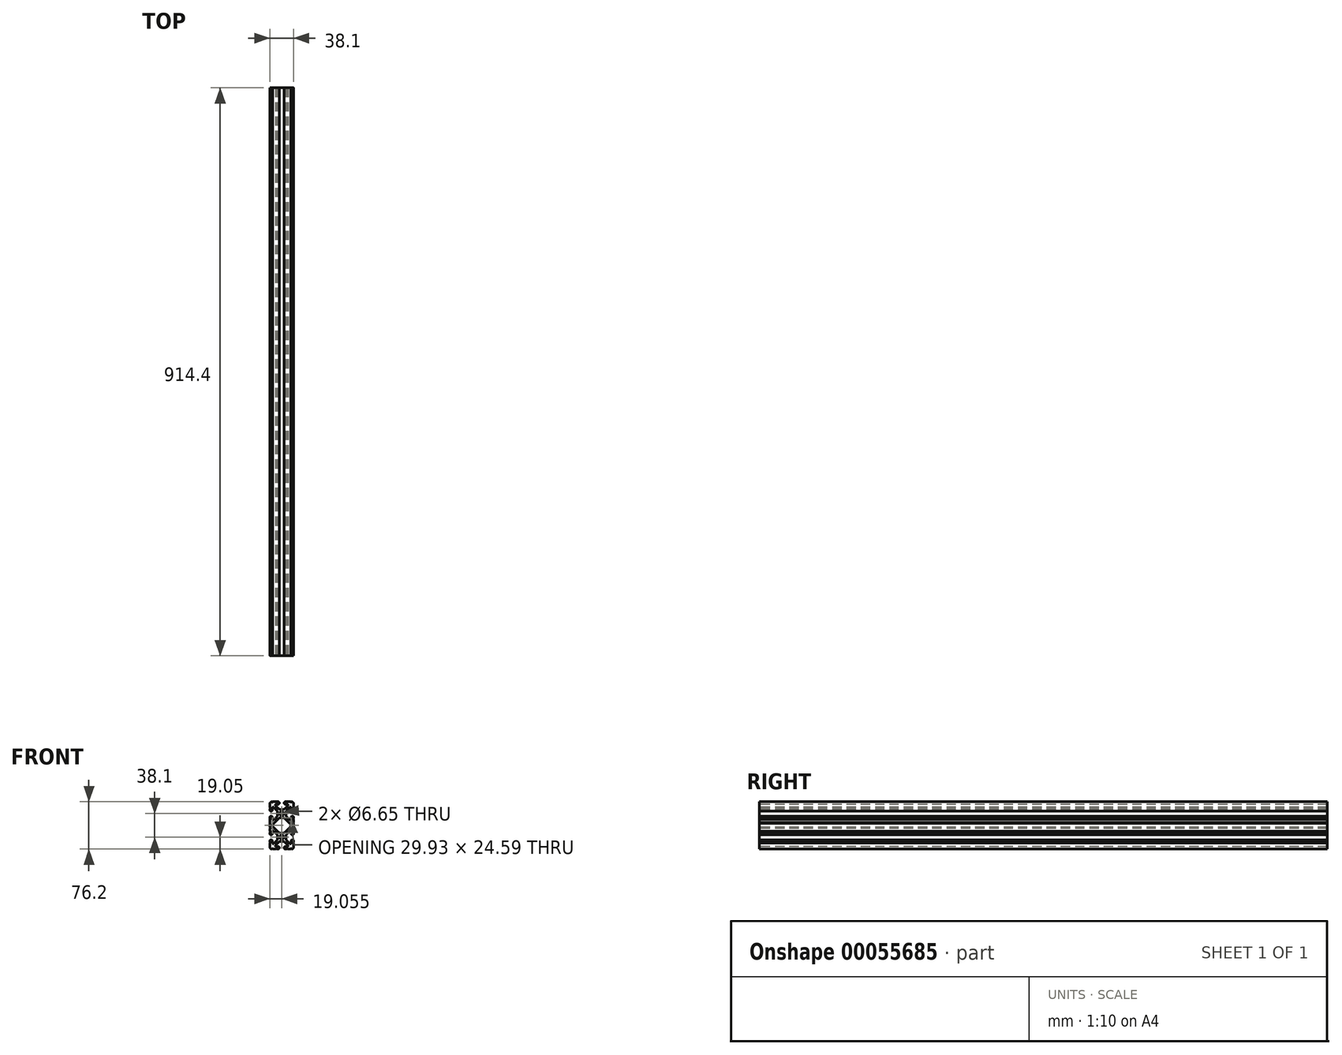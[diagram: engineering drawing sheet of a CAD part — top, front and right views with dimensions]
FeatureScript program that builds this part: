
annotation { "Feature Type Name" : "Feature", "Feature Type Description" : "" }
export const myFeature = defineFeature(function(context is Context, id is Id, definition is map)
    precondition{}
    {
        {
            var Q0;
            Q0=qCreatedBy(makeId("Front.planeOp"),FACE);
            var sketch = newSketch(context, id + "F0", { "sketchPlane" : qUnion([Q0])});
            skLineSegment(sketch, "E0", {"start": v(-110.84, 69.05) * mm, "end": v(-103.85, 69.05) * mm});
            skLineSegment(sketch, "E1", {"start": v(-107.35, 65.56) * mm, "end": v(-107.35, 72.54) * mm});
            skLineSegment(sketch, "E2", {"start": v(-110.84, 30.95) * mm, "end": v(-103.85, 30.95) * mm});
            skLineSegment(sketch, "E3", {"start": v(-107.35, 27.46) * mm, "end": v(-107.35, 34.44) * mm});
            skLineSegment(sketch, "E4", {"start": v(-89.1, 46.04) * mm, "end": v(-87.5, 46.04) * mm});
            skLineSegment(sketch, "E5", {"start": v(-88.3, 45.24) * mm, "end": v(-88.3, 46.84) * mm});
            skLineSegment(sketch, "E6", {"start": v(-99.4, 88.1) * mm, "end": v(-97.8, 88.1) * mm});
            skLineSegment(sketch, "E7", {"start": v(-98.6, 87.3) * mm, "end": v(-98.6, 88.9) * mm});
            skLineSegment(sketch, "E8", {"start": v(-127.2, 15.86) * mm, "end": v(-125.6, 15.86) * mm});
            skLineSegment(sketch, "E9", {"start": v(-126.4, 15.06) * mm, "end": v(-126.4, 16.66) * mm});
            skLineSegment(sketch, "E10", {"start": v(-89.1, 77.79) * mm, "end": v(-87.5, 77.79) * mm});
            skLineSegment(sketch, "E11", {"start": v(-88.3, 76.99) * mm, "end": v(-88.3, 78.59) * mm});
            skLineSegment(sketch, "E12", {"start": v(-127.2, 60.31) * mm, "end": v(-125.6, 60.31) * mm});
            skLineSegment(sketch, "E13", {"start": v(-126.4, 59.51) * mm, "end": v(-126.4, 61.11) * mm});
            skLineSegment(sketch, "E14", {"start": v(-89.1, 84.14) * mm, "end": v(-87.5, 84.14) * mm});
            skLineSegment(sketch, "E15", {"start": v(-88.3, 83.34) * mm, "end": v(-88.3, 84.94) * mm});
            skLineSegment(sketch, "E16", {"start": v(-127.2, 84.14) * mm, "end": v(-125.6, 84.14) * mm});
            skLineSegment(sketch, "E17", {"start": v(-126.4, 83.34) * mm, "end": v(-126.4, 84.94) * mm});
            skLineSegment(sketch, "E18", {"start": v(-127.2, 53.96) * mm, "end": v(-125.6, 53.96) * mm});
            skLineSegment(sketch, "E19", {"start": v(-126.4, 53.16) * mm, "end": v(-126.4, 54.76) * mm});
            skLineSegment(sketch, "E20", {"start": v(-116.88, 88.1) * mm, "end": v(-115.28, 88.1) * mm});
            skLineSegment(sketch, "E21", {"start": v(-116.08, 87.3) * mm, "end": v(-116.08, 88.9) * mm});
            skLineSegment(sketch, "E22", {"start": v(-89.1, 15.86) * mm, "end": v(-87.5, 15.86) * mm});
            skLineSegment(sketch, "E23", {"start": v(-88.3, 15.06) * mm, "end": v(-88.3, 16.66) * mm});
            skArc(sketch, "E24", {"start": v(-109.26, 62.3) * mm, "mid": v(-111.08, 61.93) * mm, "end": v(-112.62, 60.9) * mm});
            skLineSegment(sketch, "E25", {"start": v(-112.62, 60.9) * mm, "end": v(-121.46, 52.07) * mm});
            skArc(sketch, "E26", {"start": v(-121.46, 52.07) * mm, "mid": v(-122.31, 50) * mm, "end": v(-121.46, 47.93) * mm});
            skLineSegment(sketch, "E27", {"start": v(-121.46, 47.93) * mm, "end": v(-112.62, 39.1) * mm});
            skArc(sketch, "E28", {"start": v(-112.62, 39.1) * mm, "mid": v(-111.08, 38.07) * mm, "end": v(-109.26, 37.7) * mm});
            skLineSegment(sketch, "E29", {"start": v(-109.26, 37.7) * mm, "end": v(-105.43, 37.7) * mm});
            skArc(sketch, "E30", {"start": v(-105.43, 37.7) * mm, "mid": v(-103.61, 38.07) * mm, "end": v(-102.07, 39.1) * mm});
            skLineSegment(sketch, "E31", {"start": v(-102.07, 39.1) * mm, "end": v(-93.23, 47.93) * mm});
            skArc(sketch, "E32", {"start": v(-93.23, 47.93) * mm, "mid": v(-92.38, 50) * mm, "end": v(-93.23, 52.07) * mm});
            skLineSegment(sketch, "E33", {"start": v(-93.23, 52.07) * mm, "end": v(-102.07, 60.9) * mm});
            skArc(sketch, "E34", {"start": v(-102.07, 60.9) * mm, "mid": v(-103.61, 61.93) * mm, "end": v(-105.43, 62.3) * mm});
            skArc(sketch, "E35", {"start": v(-123.2, 88.1) * mm, "mid": v(-122.43, 87.34) * mm, "end": v(-121.67, 88.1) * mm});
            skLineSegment(sketch, "E36", {"start": v(-116.84, 88.1) * mm, "end": v(-121.67, 88.1) * mm});
            skArc(sketch, "E37", {"start": v(-116.84, 88.1) * mm, "mid": v(-116.08, 87.34) * mm, "end": v(-115.32, 88.1) * mm});
            skLineSegment(sketch, "E38", {"start": v(-112.98, 88.1) * mm, "end": v(-115.32, 88.1) * mm});
            skArc(sketch, "E39", {"start": v(-111.4, 86.53) * mm, "mid": v(-111.87, 87.64) * mm, "end": v(-112.98, 88.1) * mm});
            skLineSegment(sketch, "E40", {"start": v(-111.4, 85.61) * mm, "end": v(-111.4, 86.53) * mm});
            skArc(sketch, "E41", {"start": v(-112.98, 84.04) * mm, "mid": v(-111.87, 84.5) * mm, "end": v(-111.4, 85.61) * mm});
            skLineSegment(sketch, "E42", {"start": v(-116.74, 84.04) * mm, "end": v(-112.98, 84.04) * mm});
            skArc(sketch, "E43", {"start": v(-116.74, 84.04) * mm, "mid": v(-117.37, 83.78) * mm, "end": v(-117.63, 83.15) * mm});
            skLineSegment(sketch, "E44", {"start": v(-117.63, 82.58) * mm, "end": v(-117.63, 83.15) * mm});
            skArc(sketch, "E45", {"start": v(-117.63, 82.58) * mm, "mid": v(-117.56, 82.24) * mm, "end": v(-117.37, 81.95) * mm});
            skLineSegment(sketch, "E46", {"start": v(-112.62, 77.2) * mm, "end": v(-117.37, 81.95) * mm});
            skArc(sketch, "E47", {"start": v(-112.62, 77.2) * mm, "mid": v(-111.08, 76.17) * mm, "end": v(-109.26, 75.8) * mm});
            skLineSegment(sketch, "E48", {"start": v(-105.43, 75.8) * mm, "end": v(-109.26, 75.8) * mm});
            skArc(sketch, "E49", {"start": v(-105.43, 75.8) * mm, "mid": v(-103.61, 76.17) * mm, "end": v(-102.07, 77.2) * mm});
            skLineSegment(sketch, "E50", {"start": v(-97.32, 81.95) * mm, "end": v(-102.07, 77.2) * mm});
            skArc(sketch, "E51", {"start": v(-97.32, 81.95) * mm, "mid": v(-97.13, 82.24) * mm, "end": v(-97.06, 82.58) * mm});
            skLineSegment(sketch, "E52", {"start": v(-97.06, 83.15) * mm, "end": v(-97.06, 82.58) * mm});
            skArc(sketch, "E53", {"start": v(-97.06, 83.15) * mm, "mid": v(-97.32, 83.78) * mm, "end": v(-97.95, 84.04) * mm});
            skLineSegment(sketch, "E54", {"start": v(-101.7, 84.04) * mm, "end": v(-97.95, 84.04) * mm});
            skArc(sketch, "E55", {"start": v(-103.28, 85.61) * mm, "mid": v(-102.82, 84.5) * mm, "end": v(-101.7, 84.04) * mm});
            skLineSegment(sketch, "E56", {"start": v(-103.28, 86.53) * mm, "end": v(-103.28, 85.61) * mm});
            skArc(sketch, "E57", {"start": v(-101.7, 88.1) * mm, "mid": v(-102.82, 87.64) * mm, "end": v(-103.28, 86.53) * mm});
            skLineSegment(sketch, "E58", {"start": v(-99.37, 88.1) * mm, "end": v(-101.7, 88.1) * mm});
            skArc(sketch, "E59", {"start": v(-99.37, 88.1) * mm, "mid": v(-98.6, 87.34) * mm, "end": v(-97.85, 88.1) * mm});
            skLineSegment(sketch, "E60", {"start": v(-93.02, 88.1) * mm, "end": v(-97.85, 88.1) * mm});
            skArc(sketch, "E61", {"start": v(-93.02, 88.1) * mm, "mid": v(-92.26, 87.34) * mm, "end": v(-91.5, 88.1) * mm});
            skArc(sketch, "E62", {"start": v(-88.3, 84.9) * mm, "mid": v(-89.23, 87.17) * mm, "end": v(-91.5, 88.1) * mm});
            skArc(sketch, "E63", {"start": v(-88.3, 84.9) * mm, "mid": v(-89.06, 84.14) * mm, "end": v(-88.3, 83.38) * mm});
            skLineSegment(sketch, "E64", {"start": v(-88.3, 78.55) * mm, "end": v(-88.3, 83.38) * mm});
            skArc(sketch, "E65", {"start": v(-88.3, 78.55) * mm, "mid": v(-89.06, 77.79) * mm, "end": v(-88.3, 77.03) * mm});
            skLineSegment(sketch, "E66", {"start": v(-88.3, 74.69) * mm, "end": v(-88.3, 77.03) * mm});
            skArc(sketch, "E67", {"start": v(-89.87, 73.11) * mm, "mid": v(-88.76, 73.58) * mm, "end": v(-88.3, 74.69) * mm});
            skLineSegment(sketch, "E68", {"start": v(-90.78, 73.11) * mm, "end": v(-89.87, 73.11) * mm});
            skArc(sketch, "E69", {"start": v(-92.36, 74.69) * mm, "mid": v(-91.9, 73.58) * mm, "end": v(-90.78, 73.11) * mm});
            skLineSegment(sketch, "E70", {"start": v(-92.36, 78.45) * mm, "end": v(-92.36, 74.69) * mm});
            skArc(sketch, "E71", {"start": v(-92.36, 78.45) * mm, "mid": v(-92.62, 79.08) * mm, "end": v(-93.25, 79.34) * mm});
            skLineSegment(sketch, "E72", {"start": v(-93.82, 79.34) * mm, "end": v(-93.25, 79.34) * mm});
            skArc(sketch, "E73", {"start": v(-93.82, 79.34) * mm, "mid": v(-94.16, 79.27) * mm, "end": v(-94.44, 79.08) * mm});
            skLineSegment(sketch, "E74", {"start": v(-99.2, 74.32) * mm, "end": v(-94.44, 79.08) * mm});
            skArc(sketch, "E75", {"start": v(-99.2, 74.32) * mm, "mid": v(-100.23, 72.78) * mm, "end": v(-100.59, 70.97) * mm});
            skLineSegment(sketch, "E76", {"start": v(-100.59, 67.13) * mm, "end": v(-100.59, 70.97) * mm});
            skArc(sketch, "E77", {"start": v(-100.59, 67.13) * mm, "mid": v(-100.23, 65.32) * mm, "end": v(-99.2, 63.78) * mm});
            skLineSegment(sketch, "E78", {"start": v(-94.44, 59.02) * mm, "end": v(-99.2, 63.78) * mm});
            skArc(sketch, "E79", {"start": v(-94.44, 59.02) * mm, "mid": v(-94.16, 58.83) * mm, "end": v(-93.82, 58.76) * mm});
            skLineSegment(sketch, "E80", {"start": v(-93.25, 58.76) * mm, "end": v(-93.82, 58.76) * mm});
            skArc(sketch, "E81", {"start": v(-93.25, 58.76) * mm, "mid": v(-92.62, 59.02) * mm, "end": v(-92.36, 59.65) * mm});
            skLineSegment(sketch, "E82", {"start": v(-92.36, 63.41) * mm, "end": v(-92.36, 59.65) * mm});
            skArc(sketch, "E83", {"start": v(-90.78, 64.99) * mm, "mid": v(-91.9, 64.52) * mm, "end": v(-92.36, 63.41) * mm});
            skLineSegment(sketch, "E84", {"start": v(-89.87, 64.99) * mm, "end": v(-90.78, 64.99) * mm});
            skArc(sketch, "E85", {"start": v(-88.3, 63.41) * mm, "mid": v(-88.76, 64.52) * mm, "end": v(-89.87, 64.99) * mm});
            skLineSegment(sketch, "E86", {"start": v(-88.3, 61.07) * mm, "end": v(-88.3, 63.41) * mm});
            skArc(sketch, "E87", {"start": v(-88.3, 61.07) * mm, "mid": v(-89.06, 60.31) * mm, "end": v(-88.3, 59.55) * mm});
            skLineSegment(sketch, "E88", {"start": v(-88.3, 54.72) * mm, "end": v(-88.3, 59.55) * mm});
            skArc(sketch, "E89", {"start": v(-88.3, 54.72) * mm, "mid": v(-89.06, 53.96) * mm, "end": v(-88.3, 53.2) * mm});
            skLineSegment(sketch, "E90", {"start": v(-88.3, 46.8) * mm, "end": v(-88.3, 53.2) * mm});
            skArc(sketch, "E91", {"start": v(-88.3, 46.8) * mm, "mid": v(-89.06, 46.04) * mm, "end": v(-88.3, 45.28) * mm});
            skLineSegment(sketch, "E92", {"start": v(-88.3, 40.45) * mm, "end": v(-88.3, 45.28) * mm});
            skArc(sketch, "E93", {"start": v(-88.3, 40.45) * mm, "mid": v(-89.06, 39.69) * mm, "end": v(-88.3, 38.93) * mm});
            skLineSegment(sketch, "E94", {"start": v(-88.3, 36.59) * mm, "end": v(-88.3, 38.93) * mm});
            skArc(sketch, "E95", {"start": v(-89.87, 35.01) * mm, "mid": v(-88.76, 35.48) * mm, "end": v(-88.3, 36.59) * mm});
            skLineSegment(sketch, "E96", {"start": v(-90.78, 35.01) * mm, "end": v(-89.87, 35.01) * mm});
            skArc(sketch, "E97", {"start": v(-92.36, 36.59) * mm, "mid": v(-91.9, 35.48) * mm, "end": v(-90.78, 35.01) * mm});
            skLineSegment(sketch, "E98", {"start": v(-92.36, 40.35) * mm, "end": v(-92.36, 36.59) * mm});
            skArc(sketch, "E99", {"start": v(-92.36, 40.35) * mm, "mid": v(-92.62, 40.98) * mm, "end": v(-93.25, 41.24) * mm});
            skLineSegment(sketch, "E100", {"start": v(-93.82, 41.24) * mm, "end": v(-93.25, 41.24) * mm});
            skArc(sketch, "E101", {"start": v(-93.82, 41.24) * mm, "mid": v(-94.16, 41.17) * mm, "end": v(-94.44, 40.98) * mm});
            skLineSegment(sketch, "E102", {"start": v(-99.2, 36.22) * mm, "end": v(-94.44, 40.98) * mm});
            skArc(sketch, "E103", {"start": v(-99.2, 36.22) * mm, "mid": v(-100.23, 34.68) * mm, "end": v(-100.59, 32.87) * mm});
            skLineSegment(sketch, "E104", {"start": v(-100.59, 29.03) * mm, "end": v(-100.59, 32.87) * mm});
            skArc(sketch, "E105", {"start": v(-100.59, 29.03) * mm, "mid": v(-100.23, 27.22) * mm, "end": v(-99.2, 25.68) * mm});
            skLineSegment(sketch, "E106", {"start": v(-94.44, 20.92) * mm, "end": v(-99.2, 25.68) * mm});
            skArc(sketch, "E107", {"start": v(-94.44, 20.92) * mm, "mid": v(-94.16, 20.73) * mm, "end": v(-93.82, 20.66) * mm});
            skLineSegment(sketch, "E108", {"start": v(-93.25, 20.66) * mm, "end": v(-93.82, 20.66) * mm});
            skArc(sketch, "E109", {"start": v(-93.25, 20.66) * mm, "mid": v(-92.62, 20.92) * mm, "end": v(-92.36, 21.55) * mm});
            skLineSegment(sketch, "E110", {"start": v(-92.36, 25.31) * mm, "end": v(-92.36, 21.55) * mm});
            skArc(sketch, "E111", {"start": v(-90.78, 26.89) * mm, "mid": v(-91.9, 26.42) * mm, "end": v(-92.36, 25.31) * mm});
            skLineSegment(sketch, "E112", {"start": v(-89.87, 26.89) * mm, "end": v(-90.78, 26.89) * mm});
            skArc(sketch, "E113", {"start": v(-88.3, 25.31) * mm, "mid": v(-88.76, 26.42) * mm, "end": v(-89.87, 26.89) * mm});
            skLineSegment(sketch, "E114", {"start": v(-88.3, 22.97) * mm, "end": v(-88.3, 25.31) * mm});
            skArc(sketch, "E115", {"start": v(-88.3, 22.97) * mm, "mid": v(-89.06, 22.21) * mm, "end": v(-88.3, 21.45) * mm});
            skLineSegment(sketch, "E116", {"start": v(-88.3, 16.62) * mm, "end": v(-88.3, 21.45) * mm});
            skArc(sketch, "E117", {"start": v(-88.3, 16.62) * mm, "mid": v(-89.06, 15.86) * mm, "end": v(-88.3, 15.1) * mm});
            skArc(sketch, "E118", {"start": v(-91.5, 11.9) * mm, "mid": v(-89.23, 12.83) * mm, "end": v(-88.3, 15.1) * mm});
            skArc(sketch, "E119", {"start": v(-91.5, 11.9) * mm, "mid": v(-92.26, 12.66) * mm, "end": v(-93.02, 11.9) * mm});
            skLineSegment(sketch, "E120", {"start": v(-97.85, 11.9) * mm, "end": v(-93.02, 11.9) * mm});
            skArc(sketch, "E121", {"start": v(-97.85, 11.9) * mm, "mid": v(-98.6, 12.66) * mm, "end": v(-99.37, 11.9) * mm});
            skLineSegment(sketch, "E122", {"start": v(-101.7, 11.9) * mm, "end": v(-99.37, 11.9) * mm});
            skArc(sketch, "E123", {"start": v(-103.28, 13.47) * mm, "mid": v(-102.82, 12.36) * mm, "end": v(-101.7, 11.9) * mm});
            skLineSegment(sketch, "E124", {"start": v(-103.28, 14.39) * mm, "end": v(-103.28, 13.47) * mm});
            skArc(sketch, "E125", {"start": v(-101.7, 15.96) * mm, "mid": v(-102.82, 15.5) * mm, "end": v(-103.28, 14.39) * mm});
            skLineSegment(sketch, "E126", {"start": v(-97.95, 15.96) * mm, "end": v(-101.7, 15.96) * mm});
            skArc(sketch, "E127", {"start": v(-97.95, 15.96) * mm, "mid": v(-97.32, 16.22) * mm, "end": v(-97.06, 16.85) * mm});
            skLineSegment(sketch, "E128", {"start": v(-97.06, 17.42) * mm, "end": v(-97.06, 16.85) * mm});
            skArc(sketch, "E129", {"start": v(-97.06, 17.42) * mm, "mid": v(-97.13, 17.76) * mm, "end": v(-97.32, 18.05) * mm});
            skLineSegment(sketch, "E130", {"start": v(-102.07, 22.8) * mm, "end": v(-97.32, 18.05) * mm});
            skArc(sketch, "E131", {"start": v(-102.07, 22.8) * mm, "mid": v(-103.61, 23.83) * mm, "end": v(-105.43, 24.2) * mm});
            skLineSegment(sketch, "E132", {"start": v(-109.26, 24.2) * mm, "end": v(-105.43, 24.2) * mm});
            skArc(sketch, "E133", {"start": v(-109.26, 24.2) * mm, "mid": v(-111.08, 23.83) * mm, "end": v(-112.62, 22.8) * mm});
            skLineSegment(sketch, "E134", {"start": v(-117.37, 18.05) * mm, "end": v(-112.62, 22.8) * mm});
            skArc(sketch, "E135", {"start": v(-117.37, 18.05) * mm, "mid": v(-117.56, 17.76) * mm, "end": v(-117.63, 17.42) * mm});
            skLineSegment(sketch, "E136", {"start": v(-117.63, 16.85) * mm, "end": v(-117.63, 17.42) * mm});
            skArc(sketch, "E137", {"start": v(-117.63, 16.85) * mm, "mid": v(-117.37, 16.22) * mm, "end": v(-116.74, 15.96) * mm});
            skLineSegment(sketch, "E138", {"start": v(-112.98, 15.96) * mm, "end": v(-116.74, 15.96) * mm});
            skArc(sketch, "E139", {"start": v(-111.4, 14.39) * mm, "mid": v(-111.87, 15.5) * mm, "end": v(-112.98, 15.96) * mm});
            skLineSegment(sketch, "E140", {"start": v(-111.4, 13.47) * mm, "end": v(-111.4, 14.39) * mm});
            skArc(sketch, "E141", {"start": v(-112.98, 11.9) * mm, "mid": v(-111.87, 12.36) * mm, "end": v(-111.4, 13.47) * mm});
            skLineSegment(sketch, "E142", {"start": v(-115.32, 11.9) * mm, "end": v(-112.98, 11.9) * mm});
            skArc(sketch, "E143", {"start": v(-115.32, 11.9) * mm, "mid": v(-116.08, 12.66) * mm, "end": v(-116.84, 11.9) * mm});
            skLineSegment(sketch, "E144", {"start": v(-121.67, 11.9) * mm, "end": v(-116.84, 11.9) * mm});
            skArc(sketch, "E145", {"start": v(-121.67, 11.9) * mm, "mid": v(-122.43, 12.66) * mm, "end": v(-123.2, 11.9) * mm});
            skArc(sketch, "E146", {"start": v(-126.4, 15.1) * mm, "mid": v(-125.47, 12.83) * mm, "end": v(-123.2, 11.9) * mm});
            skArc(sketch, "E147", {"start": v(-126.4, 15.1) * mm, "mid": v(-125.63, 15.86) * mm, "end": v(-126.4, 16.62) * mm});
            skLineSegment(sketch, "E148", {"start": v(-126.4, 21.45) * mm, "end": v(-126.4, 16.62) * mm});
            skArc(sketch, "E149", {"start": v(-126.4, 21.45) * mm, "mid": v(-125.63, 22.21) * mm, "end": v(-126.4, 22.97) * mm});
            skLineSegment(sketch, "E150", {"start": v(-126.4, 25.31) * mm, "end": v(-126.4, 22.97) * mm});
            skArc(sketch, "E151", {"start": v(-124.82, 26.89) * mm, "mid": v(-125.93, 26.42) * mm, "end": v(-126.4, 25.31) * mm});
            skLineSegment(sketch, "E152", {"start": v(-123.9, 26.89) * mm, "end": v(-124.82, 26.89) * mm});
            skArc(sketch, "E153", {"start": v(-122.33, 25.31) * mm, "mid": v(-122.8, 26.42) * mm, "end": v(-123.9, 26.89) * mm});
            skLineSegment(sketch, "E154", {"start": v(-122.33, 21.55) * mm, "end": v(-122.33, 25.31) * mm});
            skArc(sketch, "E155", {"start": v(-122.33, 21.55) * mm, "mid": v(-122.07, 20.92) * mm, "end": v(-121.44, 20.66) * mm});
            skLineSegment(sketch, "E156", {"start": v(-120.87, 20.66) * mm, "end": v(-121.44, 20.66) * mm});
            skArc(sketch, "E157", {"start": v(-120.87, 20.66) * mm, "mid": v(-120.53, 20.73) * mm, "end": v(-120.25, 20.92) * mm});
            skLineSegment(sketch, "E158", {"start": v(-115.5, 25.68) * mm, "end": v(-120.25, 20.92) * mm});
            skArc(sketch, "E159", {"start": v(-115.5, 25.68) * mm, "mid": v(-114.46, 27.22) * mm, "end": v(-114.1, 29.03) * mm});
            skLineSegment(sketch, "E160", {"start": v(-114.1, 32.87) * mm, "end": v(-114.1, 29.03) * mm});
            skArc(sketch, "E161", {"start": v(-114.1, 32.87) * mm, "mid": v(-114.46, 34.68) * mm, "end": v(-115.5, 36.22) * mm});
            skLineSegment(sketch, "E162", {"start": v(-120.25, 40.98) * mm, "end": v(-115.5, 36.22) * mm});
            skArc(sketch, "E163", {"start": v(-120.25, 40.98) * mm, "mid": v(-120.53, 41.17) * mm, "end": v(-120.87, 41.24) * mm});
            skLineSegment(sketch, "E164", {"start": v(-121.44, 41.24) * mm, "end": v(-120.87, 41.24) * mm});
            skArc(sketch, "E165", {"start": v(-121.44, 41.24) * mm, "mid": v(-122.07, 40.98) * mm, "end": v(-122.33, 40.35) * mm});
            skLineSegment(sketch, "E166", {"start": v(-122.33, 36.59) * mm, "end": v(-122.33, 40.35) * mm});
            skArc(sketch, "E167", {"start": v(-123.9, 35.01) * mm, "mid": v(-122.8, 35.48) * mm, "end": v(-122.33, 36.59) * mm});
            skLineSegment(sketch, "E168", {"start": v(-124.82, 35.01) * mm, "end": v(-123.9, 35.01) * mm});
            skArc(sketch, "E169", {"start": v(-126.4, 36.59) * mm, "mid": v(-125.93, 35.48) * mm, "end": v(-124.82, 35.01) * mm});
            skLineSegment(sketch, "E170", {"start": v(-126.4, 38.93) * mm, "end": v(-126.4, 36.59) * mm});
            skArc(sketch, "E171", {"start": v(-126.4, 38.93) * mm, "mid": v(-125.63, 39.69) * mm, "end": v(-126.4, 40.45) * mm});
            skLineSegment(sketch, "E172", {"start": v(-126.4, 45.28) * mm, "end": v(-126.4, 40.45) * mm});
            skArc(sketch, "E173", {"start": v(-126.4, 45.28) * mm, "mid": v(-125.63, 46.04) * mm, "end": v(-126.4, 46.8) * mm});
            skLineSegment(sketch, "E174", {"start": v(-126.4, 53.2) * mm, "end": v(-126.4, 46.8) * mm});
            skArc(sketch, "E175", {"start": v(-126.4, 53.2) * mm, "mid": v(-125.63, 53.96) * mm, "end": v(-126.4, 54.72) * mm});
            skLineSegment(sketch, "E176", {"start": v(-126.4, 59.55) * mm, "end": v(-126.4, 54.72) * mm});
            skArc(sketch, "E177", {"start": v(-126.4, 59.55) * mm, "mid": v(-125.63, 60.31) * mm, "end": v(-126.4, 61.07) * mm});
            skLineSegment(sketch, "E178", {"start": v(-126.4, 63.41) * mm, "end": v(-126.4, 61.07) * mm});
            skArc(sketch, "E179", {"start": v(-124.82, 64.99) * mm, "mid": v(-125.93, 64.52) * mm, "end": v(-126.4, 63.41) * mm});
            skLineSegment(sketch, "E180", {"start": v(-123.9, 64.99) * mm, "end": v(-124.82, 64.99) * mm});
            skArc(sketch, "E181", {"start": v(-122.33, 63.41) * mm, "mid": v(-122.8, 64.52) * mm, "end": v(-123.9, 64.99) * mm});
            skLineSegment(sketch, "E182", {"start": v(-122.33, 59.65) * mm, "end": v(-122.33, 63.41) * mm});
            skArc(sketch, "E183", {"start": v(-122.33, 59.65) * mm, "mid": v(-122.07, 59.02) * mm, "end": v(-121.44, 58.76) * mm});
            skLineSegment(sketch, "E184", {"start": v(-120.87, 58.76) * mm, "end": v(-121.44, 58.76) * mm});
            skArc(sketch, "E185", {"start": v(-120.87, 58.76) * mm, "mid": v(-120.53, 58.83) * mm, "end": v(-120.25, 59.02) * mm});
            skLineSegment(sketch, "E186", {"start": v(-115.5, 63.78) * mm, "end": v(-120.25, 59.02) * mm});
            skArc(sketch, "E187", {"start": v(-115.5, 63.78) * mm, "mid": v(-114.46, 65.32) * mm, "end": v(-114.1, 67.13) * mm});
            skLineSegment(sketch, "E188", {"start": v(-114.1, 70.97) * mm, "end": v(-114.1, 67.13) * mm});
            skArc(sketch, "E189", {"start": v(-114.1, 70.97) * mm, "mid": v(-114.46, 72.78) * mm, "end": v(-115.5, 74.32) * mm});
            skLineSegment(sketch, "E190", {"start": v(-120.25, 79.08) * mm, "end": v(-115.5, 74.32) * mm});
            skArc(sketch, "E191", {"start": v(-120.25, 79.08) * mm, "mid": v(-120.53, 79.27) * mm, "end": v(-120.87, 79.34) * mm});
            skLineSegment(sketch, "E192", {"start": v(-121.44, 79.34) * mm, "end": v(-120.87, 79.34) * mm});
            skArc(sketch, "E193", {"start": v(-121.44, 79.34) * mm, "mid": v(-122.07, 79.08) * mm, "end": v(-122.33, 78.45) * mm});
            skLineSegment(sketch, "E194", {"start": v(-122.33, 74.69) * mm, "end": v(-122.33, 78.45) * mm});
            skArc(sketch, "E195", {"start": v(-123.9, 73.11) * mm, "mid": v(-122.8, 73.58) * mm, "end": v(-122.33, 74.69) * mm});
            skLineSegment(sketch, "E196", {"start": v(-124.82, 73.11) * mm, "end": v(-123.9, 73.11) * mm});
            skArc(sketch, "E197", {"start": v(-126.4, 74.69) * mm, "mid": v(-125.93, 73.58) * mm, "end": v(-124.82, 73.11) * mm});
            skLineSegment(sketch, "E198", {"start": v(-126.4, 77.03) * mm, "end": v(-126.4, 74.69) * mm});
            skArc(sketch, "E199", {"start": v(-126.4, 77.03) * mm, "mid": v(-125.63, 77.79) * mm, "end": v(-126.4, 78.55) * mm});
            skLineSegment(sketch, "E200", {"start": v(-126.4, 83.38) * mm, "end": v(-126.4, 78.55) * mm});
            skArc(sketch, "E201", {"start": v(-126.4, 83.38) * mm, "mid": v(-125.63, 84.14) * mm, "end": v(-126.4, 84.9) * mm});
            skCircle(sketch, "E202", {"center": v(-107.35, 69.05) * mm, "radius": 3.33 * mm});
            skArc(sketch, "E203", {"start": v(-123.2, 88.1) * mm, "mid": v(-125.47, 87.17) * mm, "end": v(-126.4, 84.9) * mm});
            skCircle(sketch, "E204", {"center": v(-107.35, 30.95) * mm, "radius": 3.33 * mm});
            skLineSegment(sketch, "E205", {"start": v(-105.43, 62.3) * mm, "end": v(-109.26, 62.3) * mm});
            skSolve(sketch);
        }
        {
            var Q0;
            Q0 = qSketchRegion(id + "F0", true);
            extrude(context, id + "F1", {"entities" : qUnion([Q0]), "oppositeDirection" : true, "depth" : 914.4 * mm});
        }
        {
            var Q0;
            Q0=makeQuery(id+"F1.opExtrude","CAP_FACE",FACE,{"disambiguationData":[OSD([sQuery(id+"F0.wireOp",EDGE,"E5"),sQuery(id+"F0.wireOp",EDGE,"E6"),sQuery(id+"F0.wireOp",EDGE,"E9"),sQuery(id+"F0.wireOp",EDGE,"E11"),sQuery(id+"F0.wireOp",EDGE,"E13"),sQuery(id+"F0.wireOp",EDGE,"E15"),sQuery(id+"F0.wireOp",EDGE,"E17"),sQuery(id+"F0.wireOp",EDGE,"E19"),sQuery(id+"F0.wireOp",EDGE,"E20"),sQuery(id+"F0.wireOp",EDGE,"E23"),sQuery(id+"F0.wireOp",EDGE,"E24"),sQuery(id+"F0.wireOp",EDGE,"E25"),sQuery(id+"F0.wireOp",EDGE,"E26"),sQuery(id+"F0.wireOp",EDGE,"E27"),sQuery(id+"F0.wireOp",EDGE,"E28"),sQuery(id+"F0.wireOp",EDGE,"E29"),sQuery(id+"F0.wireOp",EDGE,"E30"),sQuery(id+"F0.wireOp",EDGE,"E31"),sQuery(id+"F0.wireOp",EDGE,"E32"),sQuery(id+"F0.wireOp",EDGE,"E33"),sQuery(id+"F0.wireOp",EDGE,"E34"),sQuery(id+"F0.wireOp",EDGE,"E35"),sQuery(id+"F0.wireOp",EDGE,"E36"),sQuery(id+"F0.wireOp",EDGE,"E38"),sQuery(id+"F0.wireOp",EDGE,"E39"),sQuery(id+"F0.wireOp",EDGE,"E40"),sQuery(id+"F0.wireOp",EDGE,"E41"),sQuery(id+"F0.wireOp",EDGE,"E42"),sQuery(id+"F0.wireOp",EDGE,"E43"),sQuery(id+"F0.wireOp",EDGE,"E44"),sQuery(id+"F0.wireOp",EDGE,"E45"),sQuery(id+"F0.wireOp",EDGE,"E46"),sQuery(id+"F0.wireOp",EDGE,"E47"),sQuery(id+"F0.wireOp",EDGE,"E48"),sQuery(id+"F0.wireOp",EDGE,"E49"),sQuery(id+"F0.wireOp",EDGE,"E50"),sQuery(id+"F0.wireOp",EDGE,"E51"),sQuery(id+"F0.wireOp",EDGE,"E52"),sQuery(id+"F0.wireOp",EDGE,"E53"),sQuery(id+"F0.wireOp",EDGE,"E54"),sQuery(id+"F0.wireOp",EDGE,"E55"),sQuery(id+"F0.wireOp",EDGE,"E56"),sQuery(id+"F0.wireOp",EDGE,"E57"),sQuery(id+"F0.wireOp",EDGE,"E58"),sQuery(id+"F0.wireOp",EDGE,"E60"),sQuery(id+"F0.wireOp",EDGE,"E61"),sQuery(id+"F0.wireOp",EDGE,"E62"),sQuery(id+"F0.wireOp",EDGE,"E64"),sQuery(id+"F0.wireOp",EDGE,"E66"),sQuery(id+"F0.wireOp",EDGE,"E67"),sQuery(id+"F0.wireOp",EDGE,"E68"),sQuery(id+"F0.wireOp",EDGE,"E69"),sQuery(id+"F0.wireOp",EDGE,"E70"),sQuery(id+"F0.wireOp",EDGE,"E71"),sQuery(id+"F0.wireOp",EDGE,"E72"),sQuery(id+"F0.wireOp",EDGE,"E73"),sQuery(id+"F0.wireOp",EDGE,"E74"),sQuery(id+"F0.wireOp",EDGE,"E75"),sQuery(id+"F0.wireOp",EDGE,"E76"),sQuery(id+"F0.wireOp",EDGE,"E77"),sQuery(id+"F0.wireOp",EDGE,"E78"),sQuery(id+"F0.wireOp",EDGE,"E79"),sQuery(id+"F0.wireOp",EDGE,"E80"),sQuery(id+"F0.wireOp",EDGE,"E81"),sQuery(id+"F0.wireOp",EDGE,"E82"),sQuery(id+"F0.wireOp",EDGE,"E83"),sQuery(id+"F0.wireOp",EDGE,"E84"),sQuery(id+"F0.wireOp",EDGE,"E85"),sQuery(id+"F0.wireOp",EDGE,"E86"),sQuery(id+"F0.wireOp",EDGE,"E87"),sQuery(id+"F0.wireOp",EDGE,"E88"),sQuery(id+"F0.wireOp",EDGE,"E89"),sQuery(id+"F0.wireOp",EDGE,"E90"),sQuery(id+"F0.wireOp",EDGE,"E92"),sQuery(id+"F0.wireOp",EDGE,"E93"),sQuery(id+"F0.wireOp",EDGE,"E94"),sQuery(id+"F0.wireOp",EDGE,"E95"),sQuery(id+"F0.wireOp",EDGE,"E96"),sQuery(id+"F0.wireOp",EDGE,"E97"),sQuery(id+"F0.wireOp",EDGE,"E98"),sQuery(id+"F0.wireOp",EDGE,"E99"),sQuery(id+"F0.wireOp",EDGE,"E100"),sQuery(id+"F0.wireOp",EDGE,"E101"),sQuery(id+"F0.wireOp",EDGE,"E102"),sQuery(id+"F0.wireOp",EDGE,"E103"),sQuery(id+"F0.wireOp",EDGE,"E104"),sQuery(id+"F0.wireOp",EDGE,"E105"),sQuery(id+"F0.wireOp",EDGE,"E106"),sQuery(id+"F0.wireOp",EDGE,"E107"),sQuery(id+"F0.wireOp",EDGE,"E108"),sQuery(id+"F0.wireOp",EDGE,"E109"),sQuery(id+"F0.wireOp",EDGE,"E110"),sQuery(id+"F0.wireOp",EDGE,"E111"),sQuery(id+"F0.wireOp",EDGE,"E112"),sQuery(id+"F0.wireOp",EDGE,"E113"),sQuery(id+"F0.wireOp",EDGE,"E114"),sQuery(id+"F0.wireOp",EDGE,"E115"),sQuery(id+"F0.wireOp",EDGE,"E116"),sQuery(id+"F0.wireOp",EDGE,"E118"),sQuery(id+"F0.wireOp",EDGE,"E119"),sQuery(id+"F0.wireOp",EDGE,"E120"),sQuery(id+"F0.wireOp",EDGE,"E121"),sQuery(id+"F0.wireOp",EDGE,"E122"),sQuery(id+"F0.wireOp",EDGE,"E123"),sQuery(id+"F0.wireOp",EDGE,"E124"),sQuery(id+"F0.wireOp",EDGE,"E125"),sQuery(id+"F0.wireOp",EDGE,"E126"),sQuery(id+"F0.wireOp",EDGE,"E127"),sQuery(id+"F0.wireOp",EDGE,"E128"),sQuery(id+"F0.wireOp",EDGE,"E129"),sQuery(id+"F0.wireOp",EDGE,"E130"),sQuery(id+"F0.wireOp",EDGE,"E131"),sQuery(id+"F0.wireOp",EDGE,"E132"),sQuery(id+"F0.wireOp",EDGE,"E133"),sQuery(id+"F0.wireOp",EDGE,"E134"),sQuery(id+"F0.wireOp",EDGE,"E135"),sQuery(id+"F0.wireOp",EDGE,"E136"),sQuery(id+"F0.wireOp",EDGE,"E137"),sQuery(id+"F0.wireOp",EDGE,"E138"),sQuery(id+"F0.wireOp",EDGE,"E139"),sQuery(id+"F0.wireOp",EDGE,"E140"),sQuery(id+"F0.wireOp",EDGE,"E141"),sQuery(id+"F0.wireOp",EDGE,"E142"),sQuery(id+"F0.wireOp",EDGE,"E143"),sQuery(id+"F0.wireOp",EDGE,"E144"),sQuery(id+"F0.wireOp",EDGE,"E145"),sQuery(id+"F0.wireOp",EDGE,"E146"),sQuery(id+"F0.wireOp",EDGE,"E148"),sQuery(id+"F0.wireOp",EDGE,"E149"),sQuery(id+"F0.wireOp",EDGE,"E150"),sQuery(id+"F0.wireOp",EDGE,"E151"),sQuery(id+"F0.wireOp",EDGE,"E152"),sQuery(id+"F0.wireOp",EDGE,"E153"),sQuery(id+"F0.wireOp",EDGE,"E154"),sQuery(id+"F0.wireOp",EDGE,"E155"),sQuery(id+"F0.wireOp",EDGE,"E156"),sQuery(id+"F0.wireOp",EDGE,"E157"),sQuery(id+"F0.wireOp",EDGE,"E158"),sQuery(id+"F0.wireOp",EDGE,"E159"),sQuery(id+"F0.wireOp",EDGE,"E160"),sQuery(id+"F0.wireOp",EDGE,"E161"),sQuery(id+"F0.wireOp",EDGE,"E162"),sQuery(id+"F0.wireOp",EDGE,"E163"),sQuery(id+"F0.wireOp",EDGE,"E164"),sQuery(id+"F0.wireOp",EDGE,"E165"),sQuery(id+"F0.wireOp",EDGE,"E166"),sQuery(id+"F0.wireOp",EDGE,"E167"),sQuery(id+"F0.wireOp",EDGE,"E168"),sQuery(id+"F0.wireOp",EDGE,"E169"),sQuery(id+"F0.wireOp",EDGE,"E170"),sQuery(id+"F0.wireOp",EDGE,"E171"),sQuery(id+"F0.wireOp",EDGE,"E172"),sQuery(id+"F0.wireOp",EDGE,"E173"),sQuery(id+"F0.wireOp",EDGE,"E174"),sQuery(id+"F0.wireOp",EDGE,"E176"),sQuery(id+"F0.wireOp",EDGE,"E178"),sQuery(id+"F0.wireOp",EDGE,"E179"),sQuery(id+"F0.wireOp",EDGE,"E180"),sQuery(id+"F0.wireOp",EDGE,"E181"),sQuery(id+"F0.wireOp",EDGE,"E182"),sQuery(id+"F0.wireOp",EDGE,"E183"),sQuery(id+"F0.wireOp",EDGE,"E184"),sQuery(id+"F0.wireOp",EDGE,"E185"),sQuery(id+"F0.wireOp",EDGE,"E186"),sQuery(id+"F0.wireOp",EDGE,"E187"),sQuery(id+"F0.wireOp",EDGE,"E188"),sQuery(id+"F0.wireOp",EDGE,"E189"),sQuery(id+"F0.wireOp",EDGE,"E190"),sQuery(id+"F0.wireOp",EDGE,"E191"),sQuery(id+"F0.wireOp",EDGE,"E192"),sQuery(id+"F0.wireOp",EDGE,"E193"),sQuery(id+"F0.wireOp",EDGE,"E194"),sQuery(id+"F0.wireOp",EDGE,"E195"),sQuery(id+"F0.wireOp",EDGE,"E196"),sQuery(id+"F0.wireOp",EDGE,"E197"),sQuery(id+"F0.wireOp",EDGE,"E198"),sQuery(id+"F0.wireOp",EDGE,"E199"),sQuery(id+"F0.wireOp",EDGE,"E200"),sQuery(id+"F0.wireOp",EDGE,"E202"),sQuery(id+"F0.wireOp",EDGE,"E203"),sQuery(id+"F0.wireOp",EDGE,"E204"),sQuery(id+"F0.wireOp",EDGE,"E205")])],"isStart":false});
            var sketch = newSketch(context, id + "F2", { "sketchPlane" : qUnion([Q0])});
            skLineSegment(sketch, "E206", {"start": v(112.98, 11.9) * mm, "end": v(101.7, 11.9) * mm});
            skPoint(sketch, "E207", {"position": v(107.35, 11.9) * mm});
            skSolve(sketch);
        }
    });
